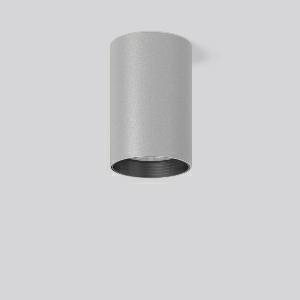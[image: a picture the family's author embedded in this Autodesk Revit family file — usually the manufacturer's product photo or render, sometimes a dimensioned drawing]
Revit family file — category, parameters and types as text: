
# Revit family: heledon_maxi_a_931228_004_deb8
name_source: partatom
category: Lighting Fixtures
units: mm (PartAtom-declared; Revit-internal decimal feet)

## family parameters
Cut with Voids When Loaded = No
Host = Face
Light Source = No
Part Type = Normal
Room Calculation Point = No
Round Connector Dimension = Use Diameter
Shared = No

## types (1)
- HELEDON maxi A (1 x LED Modul 930, 3500 lm, 3000)
    Apparent Load = 35 VA
    Approval mark = CE
    CIE Flux Codes = 96 100 100 100 100
    Color Rendering = 90
    Color Temperature = 3000
    Default Elevation = 1800 mm
    Description = Series: HELEDON maxi
Cylindrical surface-mounted downlight. Housing: die-cast aluminium, powder-coated. Internal ceiling frame polycarbonate with bayonet mounting. Black plastic ring and recessed LED to prevent glare from the side. Optical assembly with lens made of plastic (polycarbonate) for the best homogeneous light distribution - can be changed without tools. Best colour rendering index Ra>90. Suitable for Ceiling mounting. Easy installation with a separate ceiling frame with bayonet mounting and plug connection. Driver integrated. Connected via plug-in connector. High quality converter without flickering and stroboscopic effect. The following accessories can be mounted without use of tools: interchangeable lenses, decorative glasses, honeycomb louvre, clear and frosted diffusers, white interchangeable plastic ring. 
Colour: silver
Diameter: 123 mm
Height: 183 mm
Lamp: LED
Socket: without socket
Colour temperature: 3000K
Colour rendering index (CRI): 92
System power: 35 W
Rated luminous flux: 3500 lm
Luminous efficiency: 100 lm/W
Control gear: Regulated power supply
Protection class: I
Type of protection: IP 20
    Height = 183 mm
    Lamp = 1 x LED Modul 930
    Lamp Light Flux = 3500 lm
    Lamp count = 1
    Length = 123 mm
    Lifetime = 50000 h
    Luminous efficacy = 100 lm/W
    Manufacturer = RZB
    ModVariant = No
    Model = 931228.004
    Mounting Place = Ceiling
    Mounting Type = Surface mounted
    Number of Poles = 1
    OnlyDefault = Yes
    Power Factor = 1
    Product Name = HELEDON maxi A
    Product group = Surface mounted downlights
    ProductGroupID = 302
    Protection Class = Protection class I
    Protection Degree = IP 20
    RLX_Detail_Level = 1
    RLX_Emergency_Light_Flux = 0 lm
    RLX_Emergency_Type = 0
    RLX_Emergency_Type_DB = No
    RlxData = <blob elided: 98017 chars, md5=8684d1b7>
    Socket = socket
    Standby Power = 0 W
    System Light Flux = 3500 lm
    System Power = 35 W
    Type Comments = Product without accessories
    Type Image = 931193.004.jpg
    URL = http://relux.com
    VarID = ---
    Voltage = 230 V
    Voltage Range = 220-240 V
    Weight = 0.00 kg
    Width = 0 mm  [stored 0 ft]

note: [stored X ft] marks values corroborated as IEEE doubles in the binary element streams (Revit-internal decimal feet)

## geometry (parser evidence)
native form markers: Blend x4, Sweep x12
no freeform markers — native parametric forms only
